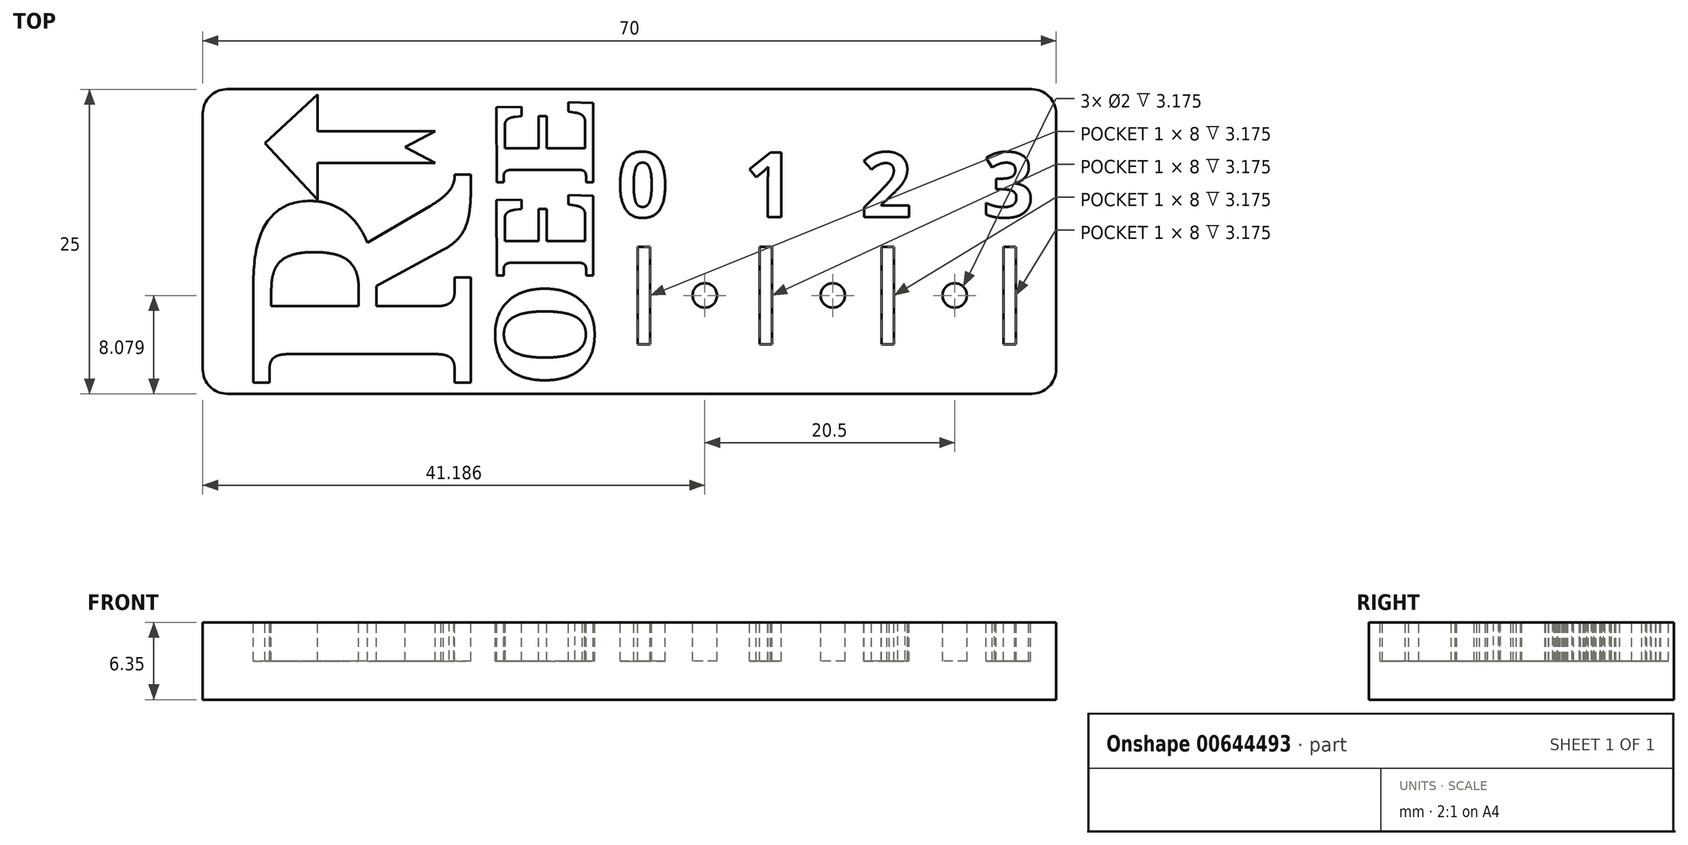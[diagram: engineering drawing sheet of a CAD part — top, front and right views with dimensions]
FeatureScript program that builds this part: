
annotation { "Feature Type Name" : "Feature", "Feature Type Description" : "" }
export const myFeature = defineFeature(function(context is Context, id is Id, definition is map)
    precondition{}
    {
        {
            var Q0;
            Q0=qCreatedBy(makeId("Top.planeOp"),FACE);
            var sketch = newSketch(context, id + "F0", { "sketchPlane" : qUnion([Q0])});
            skLineSegment(sketch, "E0.bottom", {"start": v(-55.27, 9.73) * mm, "end": v(10.73, 9.73) * mm});
            skLineSegment(sketch, "E0.top", {"start": v(-55.27, -15.27) * mm, "end": v(10.73, -15.27) * mm});
            skLineSegment(sketch, "E0.left", {"start": v(-57.27, 7.73) * mm, "end": v(-57.27, -13.27) * mm});
            skLineSegment(sketch, "E0.right", {"start": v(12.73, 7.73) * mm, "end": v(12.73, -13.27) * mm});
            skPoint(sketch, "E1.visualSharp", {"position": v(-57.27, 9.73) * mm});
            skArc(sketch, "E1.filletArc", {"start": v(-55.27, 9.73) * mm, "mid": v(-56.68, 9.15) * mm, "end": v(-57.27, 7.73) * mm});
            skPoint(sketch, "E2.visualSharp", {"position": v(12.73, 9.73) * mm});
            skArc(sketch, "E2.filletArc", {"start": v(12.73, 7.73) * mm, "mid": v(12.14, 9.15) * mm, "end": v(10.73, 9.73) * mm});
            skPoint(sketch, "E3.visualSharp", {"position": v(12.73, -15.27) * mm});
            skArc(sketch, "E3.filletArc", {"start": v(10.73, -15.27) * mm, "mid": v(12.14, -14.68) * mm, "end": v(12.73, -13.27) * mm});
            skPoint(sketch, "E4.visualSharp", {"position": v(-57.27, -15.27) * mm});
            skArc(sketch, "E4.filletArc", {"start": v(-57.27, -13.27) * mm, "mid": v(-56.68, -14.68) * mm, "end": v(-55.27, -15.27) * mm});
            skSolve(sketch);
        }
        {
            var Q0;
            Q0=qSketchRegion(id+"F0",true);
            extrude(context, id + "F1", {"entities" : qUnion([Q0]), "depth" : 6.35 * mm, "offsetDistance" : 25.4 * mm});
        }
        {
            var Q0;
            Q0=makeQuery(id+"F1.opExtrude","CAP_FACE",FACE,{"disambiguationData":[OSD([sQuery(id+"F0.wireOp",EDGE,"E0.bottom"),sQuery(id+"F0.wireOp",EDGE,"E0.top"),sQuery(id+"F0.wireOp",EDGE,"E0.left"),sQuery(id+"F0.wireOp",EDGE,"E0.right")])],"isStart":false});
            var sketch = newSketch(context, id + "F2", { "sketchPlane" : qUnion([Q0])});
            skText(sketch, "E5", { "text": "R", "fontName": "NotoSerif-Bold.ttf"});
            skText(sketch, "E6", { "text": "O\n", "fontName": "NotoSerif-Bold.ttf"});
            skText(sketch, "E7", { "text": "E", "fontName": "NotoSerif-Bold.ttf"});
            skLineSegment(sketch, "E8.bottom", {"start": v(-21.58, -3.2) * mm, "end": v(-20.58, -3.2) * mm});
            skLineSegment(sketch, "E8.top", {"start": v(-21.58, -11.2) * mm, "end": v(-20.58, -11.2) * mm});
            skLineSegment(sketch, "E8.left", {"start": v(-21.58, -3.2) * mm, "end": v(-21.58, -11.2) * mm});
            skLineSegment(sketch, "E8.right", {"start": v(-20.58, -3.2) * mm, "end": v(-20.58, -11.2) * mm});
            skLineSegment(sketch, "E9.bottom", {"start": v(-11.58, -3.2) * mm, "end": v(-10.58, -3.2) * mm});
            skLineSegment(sketch, "E9.top", {"start": v(-11.58, -11.2) * mm, "end": v(-10.58, -11.2) * mm});
            skLineSegment(sketch, "E9.left", {"start": v(-11.58, -3.2) * mm, "end": v(-11.58, -11.2) * mm});
            skLineSegment(sketch, "E9.right", {"start": v(-10.58, -3.2) * mm, "end": v(-10.58, -11.2) * mm});
            skLineSegment(sketch, "E10.bottom", {"start": v(-1.58, -3.2) * mm, "end": v(-0.58, -3.2) * mm});
            skLineSegment(sketch, "E10.top", {"start": v(-1.58, -11.2) * mm, "end": v(-0.58, -11.2) * mm});
            skLineSegment(sketch, "E10.left", {"start": v(-1.58, -3.2) * mm, "end": v(-1.58, -11.2) * mm});
            skLineSegment(sketch, "E10.right", {"start": v(-0.58, -3.2) * mm, "end": v(-0.58, -11.2) * mm});
            skLineSegment(sketch, "E11.bottom", {"start": v(8.42, -3.2) * mm, "end": v(9.42, -3.2) * mm});
            skLineSegment(sketch, "E11.top", {"start": v(8.42, -11.2) * mm, "end": v(9.42, -11.2) * mm});
            skLineSegment(sketch, "E11.left", {"start": v(8.42, -3.2) * mm, "end": v(8.42, -11.2) * mm});
            skLineSegment(sketch, "E11.right", {"start": v(9.42, -3.2) * mm, "end": v(9.42, -11.2) * mm});
            skPoint(sketch, "E12", {"position": v(-21.08, -3.2) * mm});
            skPoint(sketch, "E13", {"position": v(-11.08, -3.2) * mm});
            skPoint(sketch, "E14", {"position": v(-1.08, -3.2) * mm});
            skCircle(sketch, "E15", {"center": v(-16.08, -7.2) * mm, "radius": 1 * mm});
            skPoint(sketch, "E16", {"position": v(-20.58, -7.2) * mm});
            skCircle(sketch, "E17", {"center": v(-5.58, -7.2) * mm, "radius": 1 * mm});
            skCircle(sketch, "E18", {"center": v(4.42, -7.2) * mm, "radius": 1 * mm});
            skPoint(sketch, "E19", {"position": v(-10.58, -7.2) * mm});
            skPoint(sketch, "E20", {"position": v(-0.58, -7.2) * mm});
            skText(sketch, "E21", { "text": "0", "fontName": "OpenSans-Bold.ttf"});
            skText(sketch, "E22", { "text": "1", "fontName": "OpenSans-Bold.ttf"});
            skText(sketch, "E23", { "text": "2", "fontName": "OpenSans-Bold.ttf"});
            skText(sketch, "E24", { "text": "3", "fontName": "OpenSans-Bold.ttf"});
            skLineSegment(sketch, "E25", {"start": v(-38.2, 3.68) * mm, "end": v(-47.86, 3.68) * mm});
            skLineSegment(sketch, "E26", {"start": v(-47.86, 3.68) * mm, "end": v(-47.86, 0.68) * mm});
            skLineSegment(sketch, "E27", {"start": v(-47.86, 0.68) * mm, "end": v(-52.16, 5.3) * mm});
            skLineSegment(sketch, "E28", {"start": v(-52.16, 5.3) * mm, "end": v(-47.86, 9.3) * mm});
            skLineSegment(sketch, "E29", {"start": v(-47.86, 9.3) * mm, "end": v(-47.86, 6.3) * mm});
            skLineSegment(sketch, "E30", {"start": v(-47.86, 6.3) * mm, "end": v(-38.2, 6.3) * mm});
            skPoint(sketch, "E31", {"position": v(-40.68, 4.98) * mm});
            skLineSegment(sketch, "E32", {"start": v(-40.68, 4.98) * mm, "end": v(-38.2, 3.68) * mm});
            skLineSegment(sketch, "E33", {"start": v(-40.68, 4.98) * mm, "end": v(-38.2, 6.3) * mm});
            skText(sketch, "E34", { "text": "E", "fontName": "NotoSerif-Bold.ttf"});
            const initialGuessF2  = {"E5": [-0.03527, -0.01504, 0, 1, 0.018], "E6": [-0.02523, -0.01477, 0, 1, 0.008], "E7": [-0.02523, -0.00585, -0.00042, 1, 0.008], "E21": [-0.0233, -0.00076, 1, 0, 0.00534], "E22": [-0.01286, -0.00076, 1, 0, 0.00534], "E23": [-0.00332, -0.00076, 1, 0, 0.00534], "E24": [0.0067, -0.00076, 1, 0, 0.00534], "E34": [-0.02523, 0.00178, -0.00042, 1, 0.008]};
            skSetInitialGuess(sketch, initialGuessF2);
            skSolve(sketch);
        }
        {
            var Q0;
            Q0=qSketchRegion(id+"F2",true);
            extrude(context, id + "F3", {"entities" : qUnion([Q0]), "operationType" : NewBodyOperationType.REMOVE, "oppositeDirection" : true, "depth" : 3.17 * mm, "offsetDistance" : 25.4 * mm});
        }
    });
